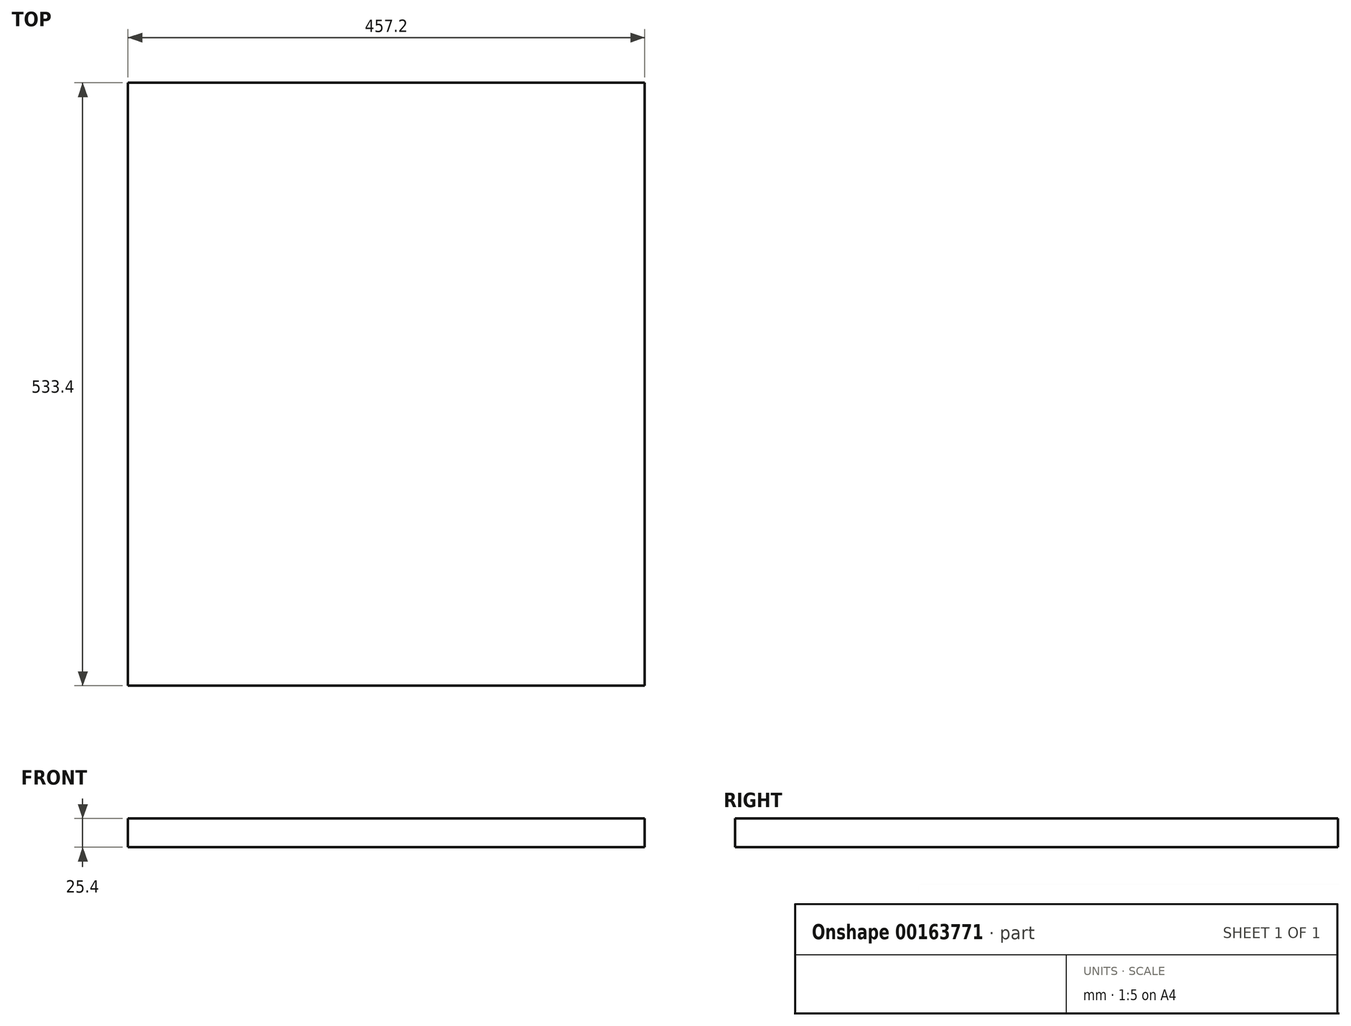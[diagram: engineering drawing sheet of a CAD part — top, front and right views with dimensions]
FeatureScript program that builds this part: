
annotation { "Feature Type Name" : "Feature", "Feature Type Description" : "" }
export const myFeature = defineFeature(function(context is Context, id is Id, definition is map)
    precondition{}
    {
        {
            var Q0;
            Q0=qCreatedBy(makeId("Top.planeOp"),FACE);
            var sketch = newSketch(context, id + "F0", { "sketchPlane" : qUnion([Q0])});
            skLineSegment(sketch, "E0.bottom", {"start": v(228.6, 266.7) * mm, "end": v(-228.6, 266.7) * mm});
            skLineSegment(sketch, "E0.top", {"start": v(228.6, -266.7) * mm, "end": v(-228.6, -266.7) * mm});
            skLineSegment(sketch, "E0.left", {"start": v(228.6, 266.7) * mm, "end": v(228.6, -266.7) * mm});
            skLineSegment(sketch, "E0.right", {"start": v(-228.6, 266.7) * mm, "end": v(-228.6, -266.7) * mm});
            skPoint(sketch, "E0.middle", {"position": v(0, 0) * mm});
            skSolve(sketch);
        }
        {
            var Q0;
            Q0=qSketchRegion(id+"F0",true);
            extrude(context, id + "F1", {"entities" : qUnion([Q0]), "depth" : 25.4 * mm, "offsetDistance" : 25.4 * mm});
        }
    });
